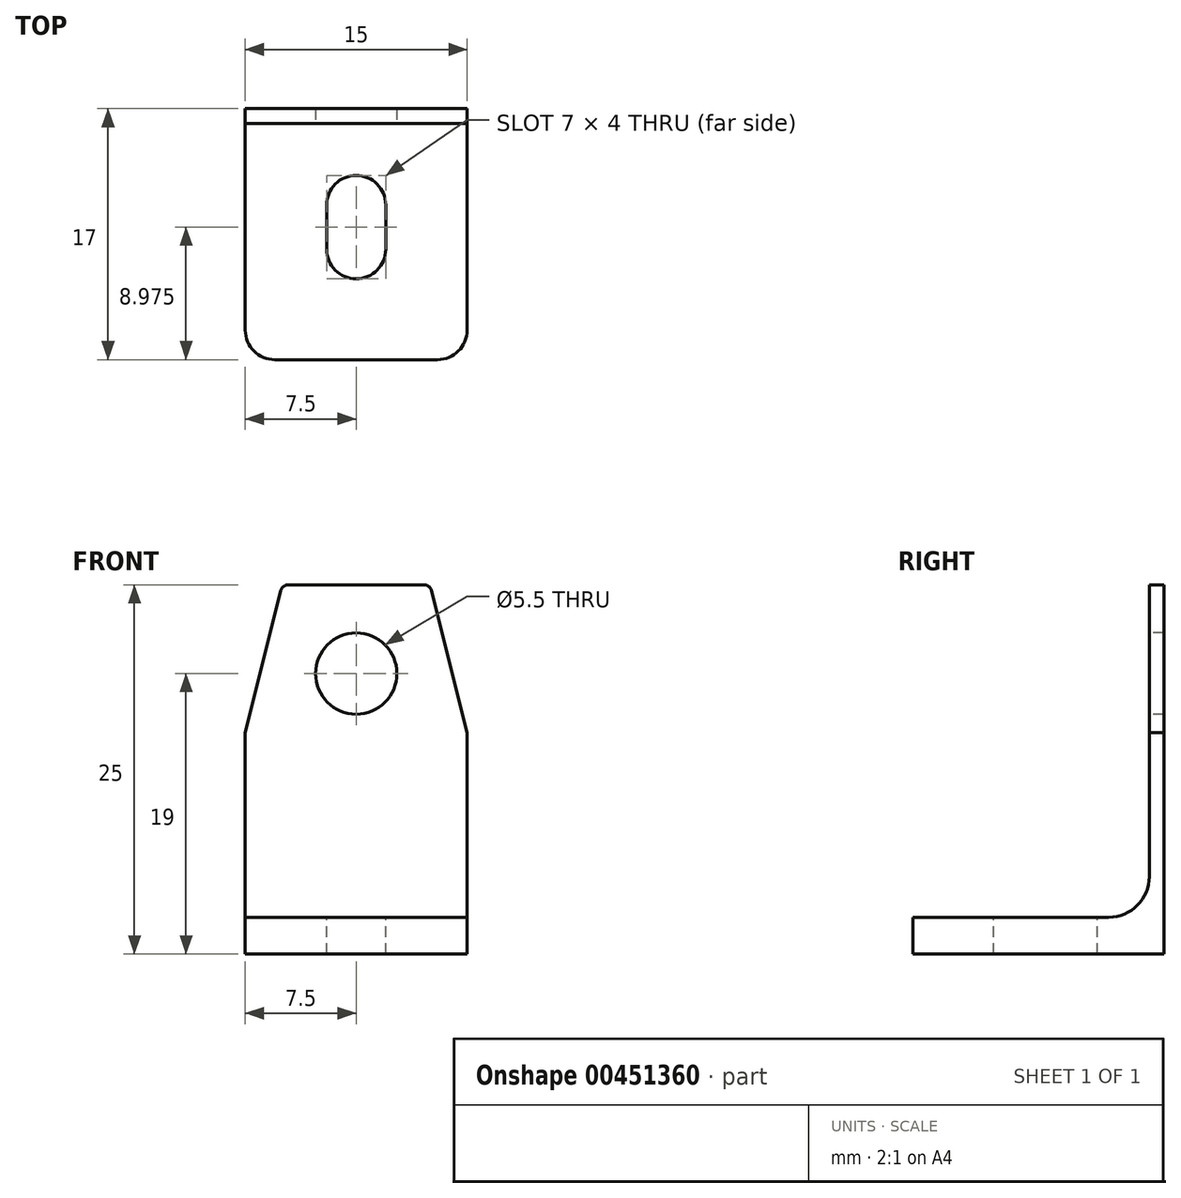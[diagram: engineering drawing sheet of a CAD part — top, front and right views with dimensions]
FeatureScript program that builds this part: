
annotation { "Feature Type Name" : "Feature", "Feature Type Description" : "" }
export const myFeature = defineFeature(function(context is Context, id is Id, definition is map)
    precondition{}
    {
        {
            var Q0;
            Q0=qCreatedBy(makeId("Right.planeOp"),FACE);
            var sketch = newSketch(context, id + "F0", { "sketchPlane" : qUnion([Q0])});
            skLineSegment(sketch, "E0", {"start": v(0, 0) * mm, "end": v(-17, 0) * mm});
            skLineSegment(sketch, "E1", {"start": v(-17, 0) * mm, "end": v(-17, 2.5) * mm});
            skLineSegment(sketch, "E2", {"start": v(-17, 2.5) * mm, "end": v(-1, 2.5) * mm});
            skLineSegment(sketch, "E3", {"start": v(-1, 2.5) * mm, "end": v(-1, 25) * mm});
            skLineSegment(sketch, "E4", {"start": v(-1, 25) * mm, "end": v(0, 25) * mm});
            skLineSegment(sketch, "E5", {"start": v(0, 25) * mm, "end": v(0, 0) * mm});
            skSolve(sketch);
        }
        {
            var Q0;
            Q0=makeQuery(id+"F0.imprint","IMPRINT",FACE,{"disambiguationData":[TD([[makeQuery(id+"F0.imprint","IMPRINT",EDGE,{"derivedFrom":sQuery(id+"F0.wireOp",EDGE,"E0")}),-1.0]])]});
            extrude(context, id + "F1", {"entities" : qUnion([Q0]), "depth" : 15 * mm});
        }
        {
            var Q0;
            Q0=makeQuery(id+"F1.opExtrude","SWEPT_EDGE",EDGE,{"disambiguationData":[OSD([sQuery(id+"F0.wireOp",EDGE,"E2"),sQuery(id+"F0.wireOp",EDGE,"E3")])]});
            fillet(context, id + "F2", {"entities" : qUnion([Q0]), "radius" : 2.75 * mm, "tangentPropagation" : true, "allowEdgeOverflow" : false});
        }
        {
            var Q0;
            Q0=makeQuery(id+"F1.opExtrude","CAP_EDGE",EDGE,{"disambiguationData":[OSD([sQuery(id+"F0.wireOp",EDGE,"E1")])],"isStart":false});
            var Q1;
            Q1=makeQuery(id+"F1.opExtrude","CAP_EDGE",EDGE,{"disambiguationData":[OSD([sQuery(id+"F0.wireOp",EDGE,"E1")])],"isStart":true});
            fillet(context, id + "F3", {"entities" : qUnion([Q0, Q1]), "radius" : 2 * mm, "tangentPropagation" : true, "allowEdgeOverflow" : false});
        }
        {
            var Q0;
            Q0=makeQuery(id+"F1.opExtrude","SWEPT_FACE",FACE,{"disambiguationData":[OSD([sQuery(id+"F0.wireOp",EDGE,"E2")])]});
            var sketch = newSketch(context, id + "F4", { "sketchPlane" : qUnion([Q0])});
            skLineSegment(sketch, "E6", {"start": v(0, -9.38) * mm, "end": v(15, -9.38) * mm, "construction": true});
            skLineSegment(sketch, "E7", {"start": v(7.5, -3.75) * mm, "end": v(7.5, -17) * mm, "construction": true});
            skLineSegment(sketch, "E8.0", {"start": v(0, -8.03) * mm, "end": v(15, -8.02) * mm, "construction": true});
            skLineSegment(sketch, "E9.bottom", {"start": v(7.5, -4.53) * mm, "end": v(7.5, -4.53) * mm});
            skLineSegment(sketch, "E9.top", {"start": v(7.5, -11.53) * mm, "end": v(7.5, -11.53) * mm});
            skLineSegment(sketch, "E9.left", {"start": v(9.5, -6.52) * mm, "end": v(9.5, -9.53) * mm});
            skLineSegment(sketch, "E9.right", {"start": v(5.5, -6.53) * mm, "end": v(5.5, -9.53) * mm});
            skPoint(sketch, "E9.middle", {"position": v(7.5, -8.03) * mm});
            skPoint(sketch, "E10.visualSharp", {"position": v(5.5, -11.53) * mm});
            skArc(sketch, "E10.filletArc", {"start": v(5.5, -9.53) * mm, "mid": v(6.09, -10.94) * mm, "end": v(7.5, -11.53) * mm});
            skPoint(sketch, "E11.visualSharp", {"position": v(9.5, -11.53) * mm});
            skArc(sketch, "E11.filletArc", {"start": v(7.5, -11.53) * mm, "mid": v(8.91, -10.94) * mm, "end": v(9.5, -9.53) * mm});
            skPoint(sketch, "E12.visualSharp", {"position": v(9.5, -4.53) * mm});
            skArc(sketch, "E12.filletArc", {"start": v(9.5, -6.52) * mm, "mid": v(8.91, -5.11) * mm, "end": v(7.5, -4.53) * mm});
            skPoint(sketch, "E13.visualSharp", {"position": v(5.5, -4.53) * mm});
            skArc(sketch, "E13.filletArc", {"start": v(7.5, -4.53) * mm, "mid": v(6.09, -5.11) * mm, "end": v(5.5, -6.53) * mm});
            skSolve(sketch);
        }
        {
            var Q0;
            Q0=makeQuery(id+"F4.imprint","IMPRINT",FACE,{"disambiguationData":[TD([[makeQuery(id+"F4.imprint","IMPRINT",EDGE,{"derivedFrom":sQuery(id+"F4.wireOp",EDGE,"E9.left")}),-1.0]])]});
            extrude(context, id + "F5", {"entities" : qUnion([Q0]), "operationType" : NewBodyOperationType.REMOVE, "oppositeDirection" : true, "depth" : 2.5 * mm});
        }
        {
            var Q0;
            Q0=makeQuery(id+"F1.opExtrude","CAP_EDGE",EDGE,{"disambiguationData":[OSD([sQuery(id+"F0.wireOp",EDGE,"E4")])],"isStart":false});
            var Q1;
            Q1=makeQuery(id+"F1.opExtrude","CAP_EDGE",EDGE,{"disambiguationData":[OSD([sQuery(id+"F0.wireOp",EDGE,"E4")])],"isStart":true});
            chamfer(context, id + "F6", {"entities" : qUnion([Q0, Q1]), "chamferType" : ChamferType.TWO_OFFSETS, "width1" : 2.5 * mm, "oppositeDirection" : false, "width2" : 10 * mm, "tangentPropagation" : true});
        }
        {
            var Q0;
            Q0=makeQuery(id+"F1.opExtrude","SWEPT_FACE",FACE,{"disambiguationData":[OSD([sQuery(id+"F0.wireOp",EDGE,"E3")])]});
            var sketch = newSketch(context, id + "F7", { "sketchPlane" : qUnion([Q0])});
            skLineSegment(sketch, "E14", {"start": v(1.25, 20) * mm, "end": v(13.75, 20) * mm, "construction": true});
            skLineSegment(sketch, "E15.0", {"start": v(1.25, 19) * mm, "end": v(13.75, 19) * mm, "construction": true});
            skCircle(sketch, "E16", {"center": v(7.5, 19) * mm, "radius": 2.75 * mm});
            skSolve(sketch);
        }
        {
            var Q0;
            Q0=makeQuery(id+"F7.imprint","IMPRINT",FACE,{"disambiguationData":[TD([[makeQuery(id+"F7.imprint","IMPRINT",EDGE,{"derivedFrom":sQuery(id+"F7.wireOp",EDGE,"E16")}),1.0]])]});
            extrude(context, id + "F8", {"entities" : qUnion([Q0]), "operationType" : NewBodyOperationType.REMOVE, "oppositeDirection" : true, "depth" : 3 * mm});
        }
        {
            var Q0;
            {var subQ0=sQuery(id+"F0.wireOp",EDGE,"E4");Q0=makeQuery(id+"F6.opChamfer","BLEND_EDGE",EDGE,{"blendedFrom":[makeQuery(id+"F1.opExtrude","CAP_EDGE",EDGE,{"disambiguationData":[OSD([subQ0])],"isStart":false}),makeQuery(id+"F1.opExtrude","SWEPT_FACE",FACE,{"disambiguationData":[OSD([subQ0])]})],"blendedInto":[makeQuery(id+"F1.opExtrude","SWEPT_FACE",FACE,{"disambiguationData":[OSD([subQ0])]})]});}
            var Q1;
            {var subQ0=sQuery(id+"F0.wireOp",EDGE,"E4");Q1=makeQuery(id+"F6.opChamfer","BLEND_EDGE",EDGE,{"blendedFrom":[makeQuery(id+"F1.opExtrude","CAP_EDGE",EDGE,{"disambiguationData":[OSD([subQ0])],"isStart":true}),makeQuery(id+"F1.opExtrude","SWEPT_FACE",FACE,{"disambiguationData":[OSD([subQ0])]})],"blendedInto":[makeQuery(id+"F1.opExtrude","SWEPT_FACE",FACE,{"disambiguationData":[OSD([subQ0])]})]});}
            fillet(context, id + "F9", {"entities" : qUnion([Q0, Q1]), "radius" : 0.5 * mm, "tangentPropagation" : true, "allowEdgeOverflow" : false});
        }
    });
